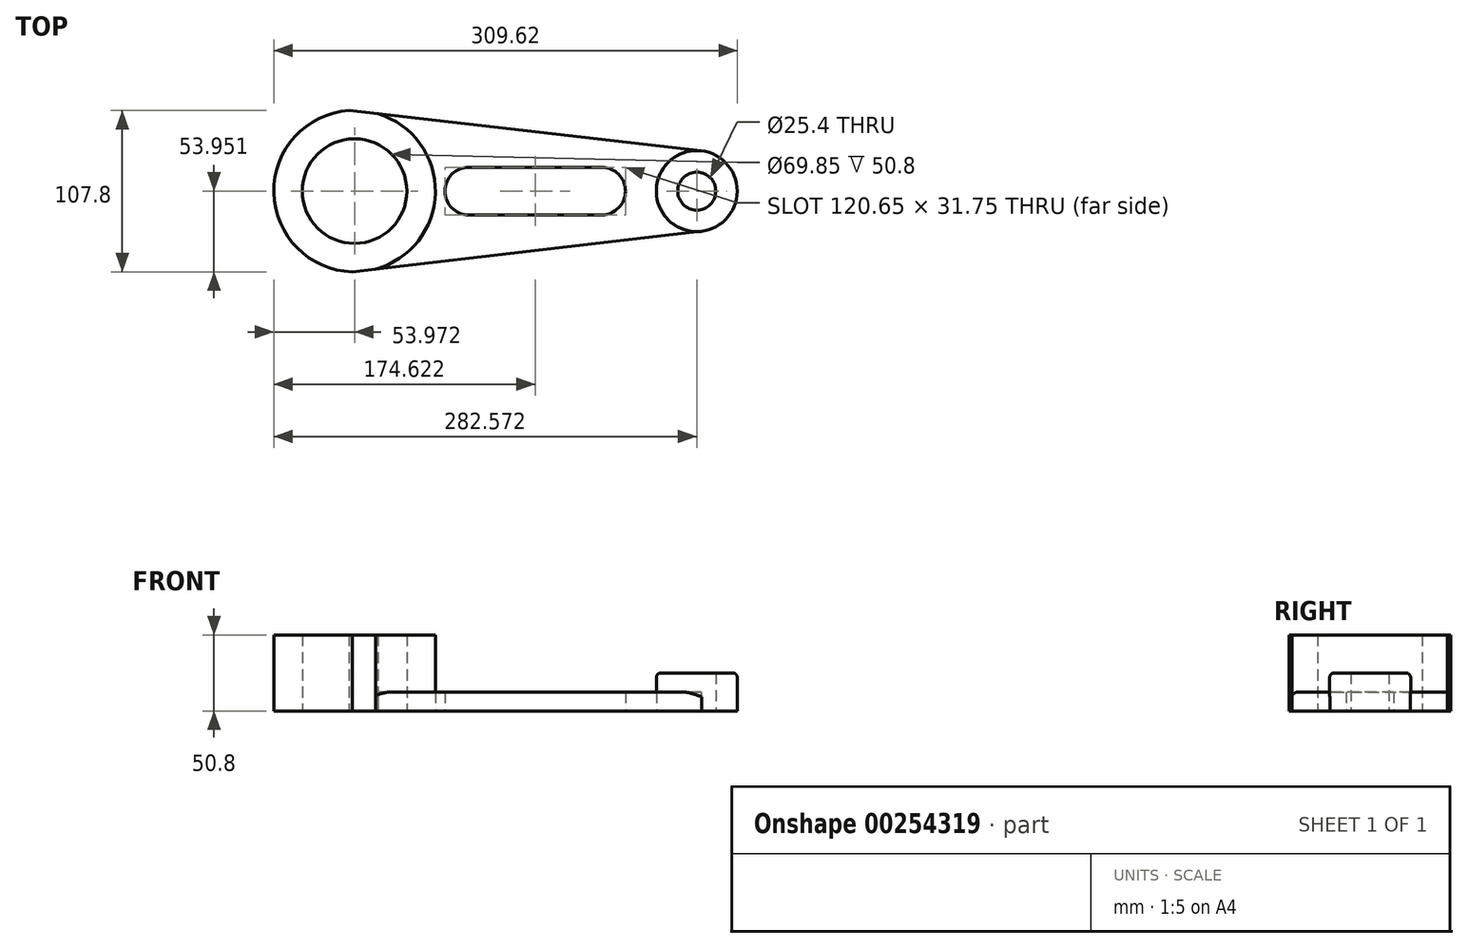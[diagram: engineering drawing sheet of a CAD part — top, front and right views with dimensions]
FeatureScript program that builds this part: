
annotation { "Feature Type Name" : "Feature", "Feature Type Description" : "" }
export const myFeature = defineFeature(function(context is Context, id is Id, definition is map)
    precondition{}
    {
        {
            var Q0;
            Q0=qCreatedBy(makeId("Top.planeOp"),FACE);
            var sketch = newSketch(context, id + "F0", { "sketchPlane" : qUnion([Q0])});
            skCircle(sketch, "E0", {"center": v(-291.59, -6.99) * mm, "radius": 53.97 * mm});
            skCircle(sketch, "E1", {"center": v(-62.99, -6.99) * mm, "radius": 27.05 * mm});
            skCircle(sketch, "E2", {"center": v(-62.99, -6.99) * mm, "radius": 12.7 * mm});
            skCircle(sketch, "E3", {"center": v(-291.59, -6.99) * mm, "radius": 34.93 * mm});
            skArc(sketch, "E4", {"start": v(-215.39, 8.89) * mm, "mid": v(-231.26, -6.99) * mm, "end": v(-215.39, -22.86) * mm});
            skArc(sketch, "E5", {"start": v(-126.49, -22.86) * mm, "mid": v(-110.61, -6.99) * mm, "end": v(-126.49, 8.89) * mm});
            skLineSegment(sketch, "E6", {"start": v(-215.39, 8.89) * mm, "end": v(-126.49, 8.89) * mm});
            skLineSegment(sketch, "E7", {"start": v(-215.39, -22.86) * mm, "end": v(-126.49, -22.86) * mm});
            skLineSegment(sketch, "E8", {"start": v(-295.3, 46.86) * mm, "end": v(-59.9, 19.89) * mm});
            skLineSegment(sketch, "E9", {"start": v(-293.18, -60.94) * mm, "end": v(-59.87, -33.86) * mm});
            skSolve(sketch);
        }
        {
            var Q0;
            Q0=makeQuery(id+"F0.imprint","IMPRINT",FACE,{"disambiguationData":[TD([[makeQuery(id+"F0.imprint","IMPRINT",EDGE,{"derivedFrom":sQuery(id+"F0.wireOp",EDGE,"E3")}),-1.0]])]});
            extrude(context, id + "F1", {"entities" : qUnion([Q0]), "depth" : 50.8 * mm});
        }
        {
            var Q0;
            Q0=makeQuery(id+"F0.imprint","IMPRINT",FACE,{"disambiguationData":[TD([[makeQuery(id+"F0.imprint","IMPRINT",EDGE,{"derivedFrom":sQuery(id+"F0.wireOp",EDGE,"E2")}),-1.0]])]});
            extrude(context, id + "F2", {"entities" : qUnion([Q0]), "depth" : 25.4 * mm});
        }
        {
            var Q0;
            Q0=makeQuery(id+"F0.imprint","IMPRINT",FACE,{"disambiguationData":[TD([[makeQuery(id+"F0.imprint","IMPRINT",EDGE,{"derivedFrom":sQuery(id+"F0.wireOp",EDGE,"E4")}),-1.0]])]});
            extrude(context, id + "F3", {"entities" : qUnion([Q0]), "depth" : 12.7 * mm});
        }
        {
            var Q0;
            {var subQ0=sQuery(id+"F0.wireOp",EDGE,"E0");Q0=makeQuery(id+"F1.opExtrude","CAP_EDGE",EDGE,{"disambiguationData":[OSD([subQ0]),TDD([makeQuery(id+"F0.imprint","IMPRINT",EDGE,{"disambiguationData":[TD([[makeQuery(id+"F0.imprint","INTERSECT",VERTEX,{"disambiguationData":[OD(1.0)],"derivedFrom":[subQ0,sQuery(id+"F0.wireOp",EDGE,"E8")]}),1.0]])],"derivedFrom":subQ0})])],"isStart":false});}
            var Q1;
            Q1=makeQuery(id+"F3.opExtrude","CAP_EDGE",EDGE,{"disambiguationData":[OSD([sQuery(id+"F0.wireOp",EDGE,"E9")])],"isStart":false});
            var Q2;
            Q2=makeQuery(id+"F2.opExtrude","CAP_EDGE",EDGE,{"disambiguationData":[OSD([sQuery(id+"F0.wireOp",EDGE,"E1")])],"isStart":false});
            fillet(context, id + "F4", {"entities" : qUnion([Q0, Q1, Q2]), "radius" : 3.17 * mm, "tangentPropagation" : true, "allowEdgeOverflow" : false});
        }
    });
